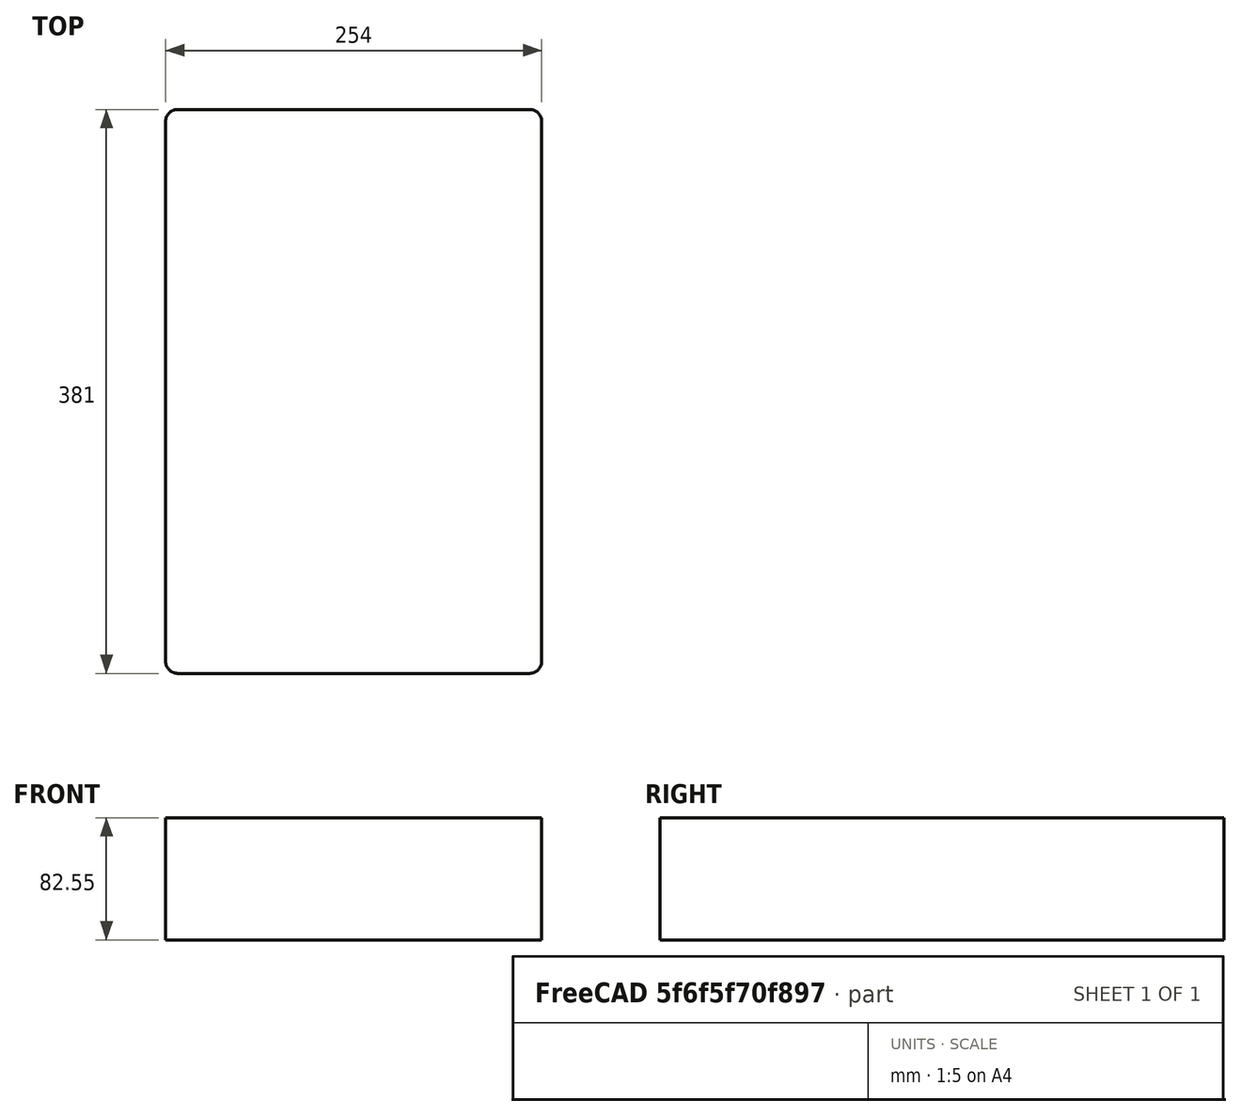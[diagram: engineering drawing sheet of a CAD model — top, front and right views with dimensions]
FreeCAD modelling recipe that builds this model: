
FCSTD DOCUMENT  (FreeCAD 0.20R29177 +426 (Git))
Label: PlayStation5
License: All rights reserved
LicenseURL: http://en.wikipedia.org/wiki/All_rights_reserved
objects: App::DocumentObjectGroup×3, PartDesign::CoordinateSystem×1, App::FeaturePython×1, Sketcher::SketchObject×1, PartDesign::Pad×1, PartDesign::Body×1, App::Part×1
note: 5 computed .brp shape members not serialized (recipe doc carries the construction recipe); baked Part::Feature solids carry a one-line shape summary decoded from their .brp

FEATURE [App::DocumentObjectGroup] Parts
FEATURE [PartDesign::CoordinateSystem] LCS_Origin
  AttacherType = Attacher::AttachEngine3D
  MapMode = 2
  Support = -> [X_Axis]
FEATURE [App::FeaturePython] Variables  # WARN: FeaturePython — macro-defined, semantics opaque (R4)
  Type = App::PropertyContainer
FEATURE [App::DocumentObjectGroup] Constraints
FEATURE [App::DocumentObjectGroup] Configurations
FEATURE [Sketcher::SketchObject] Sketch
  FullyConstrained = true
  MapMode = 5
  Support = -> [XY_Plane001]
  sketch-geometry (10):
    g0: ArcOfCircle CenterX=-119 CenterY=182.5 CenterZ=0 NormalX=0 NormalY=0 NormalZ=1 AngleXU=0 Radius=8 StartAngle=1.5708 EndAngle=3.14159
    g1: LineSegment StartX=-119 StartY=190.5 StartZ=0 EndX=119 EndY=190.5 EndZ=0
    g2: ArcOfCircle CenterX=119 CenterY=182.5 CenterZ=0 NormalX=0 NormalY=0 NormalZ=1 AngleXU=0 Radius=8 StartAngle=4.43e-14 EndAngle=1.5708
    g3: LineSegment StartX=127 StartY=182.5 StartZ=0 EndX=127 EndY=-182.5 EndZ=0
    g4: ArcOfCircle CenterX=119 CenterY=-182.5 CenterZ=0 NormalX=0 NormalY=0 NormalZ=1 AngleXU=0 Radius=8 StartAngle=4.71239 EndAngle=6.28319
    g5: LineSegment StartX=119 StartY=-190.5 StartZ=0 EndX=-119 EndY=-190.5 EndZ=0
    g6: ArcOfCircle CenterX=-119 CenterY=-182.5 CenterZ=0 NormalX=0 NormalY=0 NormalZ=1 AngleXU=0 Radius=8 StartAngle=3.14159 EndAngle=4.71239
    g7: LineSegment StartX=-127 StartY=-182.5 StartZ=0 EndX=-127 EndY=182.5 EndZ=0
    g8: GeomPoint X=-127 Y=190.5 Z=0
    g9: GeomPoint X=127 Y=-190.5 Z=0
  constraints (23):
    c: Tangent(g0,g1) = 1.5708
    c: Tangent(g1,g2) = 1.5708
    c: Tangent(g2,g3) = 1.5708
    c: Tangent(g3,g4) = 1.5708
    c: Tangent(g4,g5) = 1.5708
    c: Tangent(g5,g6) = 1.5708
    c: Tangent(g6,g7) = 1.5708
    c: Tangent(g7,g0) = 1.5708
    c: Horizontal(g1)
    c: Horizontal(g5)
    c: Vertical(g3)
    c: Vertical(g7)
    c: Equal(g0,g2)
    c: Equal(g2,g4)
    c: Equal(g4,g6)
    c: PointOnObject(g8,g1)
    c: PointOnObject(g8,g7)
    c: PointOnObject(g9,g3)
    c: PointOnObject(g9,g5)
    c: Symmetric(g4,g0,g-1)
    c: Radius(g2) = 8
    c: DistanceX(g6,g3) = 254
    c: DistanceY(g4,g1) = 381
FEATURE [PartDesign::Pad] Pad
  Direction = (0,0,1)
  Length = 82.55
  Length2 = 10
  Profile = -> Sketch
  ReferenceAxis = -> Sketch [N_Axis]
  Type = 0
FEATURE [PartDesign::Body] Body
  Group = -> [Sketch,Pad]
  Origin = -> Origin001
  Tip = -> Pad
FEATURE [App::Part] Assembly
  AssemblyType = Part::Link
  Group = -> [LCS_Origin,Variables,Constraints,Configurations,Body]
  Origin = -> Origin
  Type = Assembly
